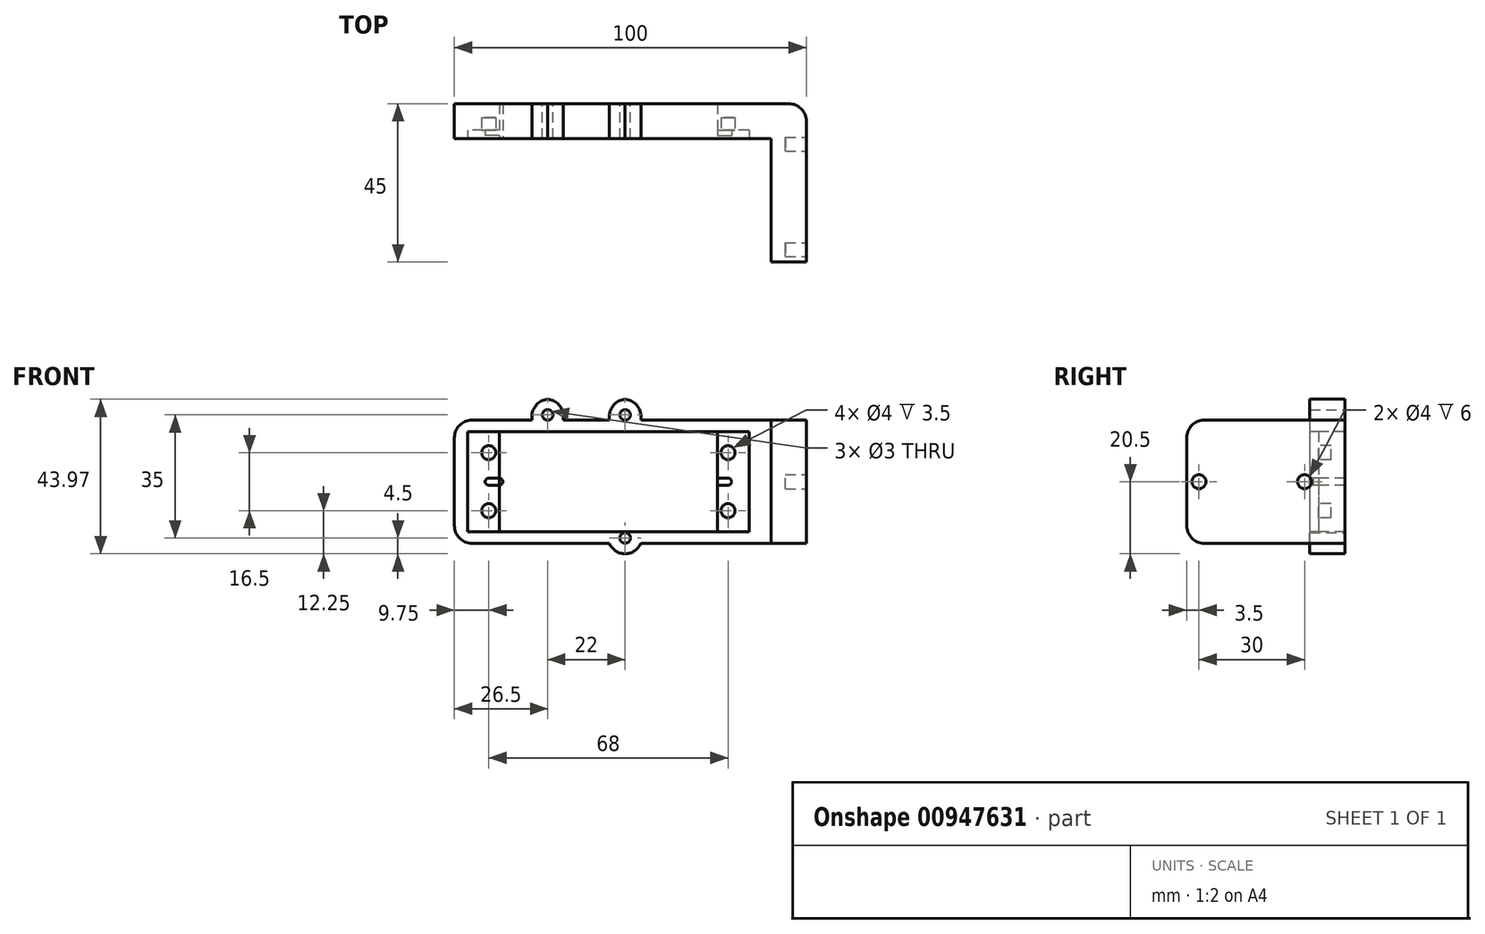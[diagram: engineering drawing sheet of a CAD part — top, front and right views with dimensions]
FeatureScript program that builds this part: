
annotation { "Feature Type Name" : "Feature", "Feature Type Description" : "" }
export const myFeature = defineFeature(function(context is Context, id is Id, definition is map)
    precondition{}
    {
        {
            assignVariable(context, id + "F0", {"name" : "thicc", "anyValue" : 10 * mm});
        }
        {
            var Q0;
            Q0=qCreatedBy(makeId("Top.planeOp"),FACE);
            var sketch = newSketch(context, id + "F1", { "sketchPlane" : qUnion([Q0])});
            skLineSegment(sketch, "E0.bottom", {"start": v(50, 22.5) * mm, "end": v(-50, 22.5) * mm});
            skLineSegment(sketch, "E0.left", {"start": v(50, 22.5) * mm, "end": v(50, -22.5) * mm});
            skPoint(sketch, "E0.middle", {"position": v(0, 0) * mm});
            skLineSegment(sketch, "E1.0", {"start": v(40, 12.5) * mm, "end": v(-50, 12.5) * mm});
            skLineSegment(sketch, "E1.1", {"start": v(40, 12.5) * mm, "end": v(40, -22.5) * mm});
            skLineSegment(sketch, "E2", {"start": v(-50, 22.5) * mm, "end": v(-50, 12.5) * mm});
            skLineSegment(sketch, "E3", {"start": v(40, -22.5) * mm, "end": v(50, -22.5) * mm});
            skSolve(sketch);
        }
        {
            var Q0;
            Q0=makeQuery(id+"F1.imprint","IMPRINT",FACE,{"disambiguationData":[TD([[makeQuery(id+"F1.imprint","IMPRINT",EDGE,{"derivedFrom":sQuery(id+"F1.wireOp",EDGE,"E0.bottom")}),1.0]])]});
            extrude(context, id + "F2", {"entities" : qUnion([Q0]), "depth" : 35 * mm, "offsetDistance" : 25 * mm});
        }
        {
            var Q0;
            Q0=makeQuery(id+"F2.opExtrude","SWEPT_FACE",FACE,{"disambiguationData":[OSD([sQuery(id+"F1.wireOp",EDGE,"E1.0")])]});
            var sketch = newSketch(context, id + "F3", { "sketchPlane" : qUnion([Q0])});
            skLineSegment(sketch, "E4.bottom", {"start": v(30.75, 3.25) * mm, "end": v(-43.25, 3.25) * mm});
            skLineSegment(sketch, "E4.top", {"start": v(30.75, 31.75) * mm, "end": v(-43.25, 31.75) * mm});
            skLineSegment(sketch, "E4.left", {"start": v(30.75, 3.25) * mm, "end": v(30.75, 31.75) * mm, "construction": true});
            skLineSegment(sketch, "E4.right", {"start": v(-43.25, 3.25) * mm, "end": v(-43.25, 31.75) * mm, "construction": true});
            skPoint(sketch, "E4.middle", {"position": v(-6.25, 17.5) * mm});
            skPoint(sketch, "E5", {"position": v(50, 17.5) * mm});
            skPoint(sketch, "E6", {"position": v(0, 0) * mm});
            skLineSegment(sketch, "E7", {"start": v(0, 0) * mm, "end": v(0, 35) * mm, "construction": true});
            skLineSegment(sketch, "E8", {"start": v(-50, 17.5) * mm, "end": v(50, 17.5) * mm, "construction": true});
            skLineSegment(sketch, "E9", {"start": v(24.75, 31.75) * mm, "end": v(24.75, 3.25) * mm});
            skLineSegment(sketch, "E10", {"start": v(-37.25, 31.75) * mm, "end": v(-37.25, 3.25) * mm});
            skLineSegment(sketch, "E11", {"start": v(24.75, 17.5) * mm, "end": v(27.75, 17.5) * mm});
            skLineSegment(sketch, "E12", {"start": v(-37.25, 17.5) * mm, "end": v(-40.25, 17.5) * mm});
            skArc(sketch, "E13.0.startCap", {"start": v(24.75, 16.5) * mm, "mid": v(23.75, 17.5) * mm, "end": v(24.75, 18.5) * mm});
            skArc(sketch, "E13.0.endCap", {"start": v(27.75, 18.5) * mm, "mid": v(28.75, 17.5) * mm, "end": v(27.75, 16.5) * mm});
            skLineSegment(sketch, "E13.0.left", {"start": v(24.75, 18.5) * mm, "end": v(27.75, 18.5) * mm});
            skLineSegment(sketch, "E13.0.right", {"start": v(24.75, 16.5) * mm, "end": v(27.75, 16.5) * mm});
            skArc(sketch, "E13.1.startCap", {"start": v(-37.25, 18.5) * mm, "mid": v(-36.25, 17.5) * mm, "end": v(-37.25, 16.5) * mm});
            skArc(sketch, "E13.1.endCap", {"start": v(-40.25, 16.5) * mm, "mid": v(-41.25, 17.5) * mm, "end": v(-40.25, 18.5) * mm});
            skLineSegment(sketch, "E13.1.left", {"start": v(-37.25, 16.5) * mm, "end": v(-40.25, 16.5) * mm});
            skLineSegment(sketch, "E13.1.right", {"start": v(-37.25, 18.5) * mm, "end": v(-40.25, 18.5) * mm});
            skCircle(sketch, "E14", {"center": v(27.75, 9.25) * mm, "radius": 2 * mm});
            skCircle(sketch, "E15", {"center": v(27.75, 25.75) * mm, "radius": 2 * mm});
            skCircle(sketch, "E16", {"center": v(-40.25, 9.25) * mm, "radius": 2 * mm});
            skCircle(sketch, "E17", {"center": v(-40.25, 25.75) * mm, "radius": 2 * mm});
            skCircle(sketch, "E18", {"center": v(-21.85, 17.5) * mm, "radius": 2.85 * mm, "construction": true});
            skLineSegment(sketch, "E19.bottom", {"start": v(-43.25, 31.75) * mm, "end": v(-46.25, 31.75) * mm});
            skLineSegment(sketch, "E19.top", {"start": v(-46.25, 3.25) * mm, "end": v(-46.25, 3.25) * mm});
            skLineSegment(sketch, "E19.right", {"start": v(-46.25, 31.75) * mm, "end": v(-46.25, 3.25) * mm});
            skLineSegment(sketch, "E20.bottom", {"start": v(30.75, 31.75) * mm, "end": v(33.75, 31.75) * mm});
            skLineSegment(sketch, "E20.top", {"start": v(27.75, 3.25) * mm, "end": v(33.75, 3.25) * mm});
            skLineSegment(sketch, "E20.right", {"start": v(33.75, 31.75) * mm, "end": v(33.75, 3.25) * mm});
            skLineSegment(sketch, "E21", {"start": v(-46.25, 3.25) * mm, "end": v(-43.25, 3.25) * mm});
            skSolve(sketch);
        }
        {
            var Q0;
            {var subQ3=sQuery(id+"F3.wireOp",EDGE,"E13.0.startCap");Q0=makeQuery(id+"F3.imprint","IMPRINT",FACE,{"disambiguationData":[TD([[makeQuery(id+"F3.imprint","IMPRINT",EDGE,{"derivedFrom":subQ3}),1.0]])]});}
            var Q1;
            {var subQ2=sQuery(id+"F3.wireOp",EDGE,"E13.1.startCap");Q1=makeQuery(id+"F3.imprint","IMPRINT",FACE,{"disambiguationData":[TD([[makeQuery(id+"F3.imprint","IMPRINT",EDGE,{"derivedFrom":subQ2}),-1.0]])]});}
            var Q2;
            {var subQ2=sQuery(id+"F3.wireOp",EDGE,"E13.0.startCap");Q2=makeQuery(id+"F3.imprint","IMPRINT",FACE,{"disambiguationData":[TD([[makeQuery(id+"F3.imprint","IMPRINT",EDGE,{"derivedFrom":subQ2}),-1.0]])]});}
            extrude(context, id + "F4", {"entities" : qUnion([Q0, Q1, Q2]), "operationType" : NewBodyOperationType.REMOVE, "endBound" : BoundingType.UP_TO_NEXT, "oppositeDirection" : true, "depth" : 25 * mm, "offsetDistance" : 25 * mm});
        }
        {
            var Q0;
            {var subQ0=sQuery(id+"F3.wireOp",EDGE,"E4.right");Q0=makeQuery(id+"F3.imprint","IMPRINT",FACE,{"disambiguationData":[TD([[makeQuery(id+"F3.imprint","IMPRINT",EDGE,{"derivedFrom":subQ0}),-1.0]])]});}
            var Q1;
            {var subQ0=sQuery(id+"F3.wireOp",EDGE,"E4.left");Q1=makeQuery(id+"F3.imprint","IMPRINT",FACE,{"disambiguationData":[TD([[makeQuery(id+"F3.imprint","IMPRINT",EDGE,{"derivedFrom":subQ0}),1.0]])]});}
            var Q2;
            Q2=makeQuery(id+"F3.imprint","IMPRINT",FACE,{"disambiguationData":[TD([[makeQuery(id+"F3.imprint","IMPRINT",EDGE,{"derivedFrom":sQuery(id+"F3.wireOp",EDGE,"E13.1.endCap")}),-1.0]])]});
            var Q3;
            Q3=makeQuery(id+"F3.imprint","IMPRINT",FACE,{"disambiguationData":[TD([[makeQuery(id+"F3.imprint","IMPRINT",EDGE,{"derivedFrom":sQuery(id+"F3.wireOp",EDGE,"E13.0.endCap")}),-1.0]])]});
            var Q4;
            Q4=makeQuery(id+"F3.imprint","IMPRINT",FACE,{"disambiguationData":[TD([[makeQuery(id+"F3.imprint","IMPRINT",EDGE,{"derivedFrom":sQuery(id+"F3.wireOp",EDGE,"E13.1.endCap")}),1.0]])]});
            var Q5;
            Q5=makeQuery(id+"F3.imprint","IMPRINT",FACE,{"disambiguationData":[TD([[makeQuery(id+"F3.imprint","IMPRINT",EDGE,{"derivedFrom":sQuery(id+"F3.wireOp",EDGE,"E13.0.endCap")}),1.0]])]});
            extrude(context, id + "F5", {"entities" : qUnion([Q0, Q1, Q2, Q3, Q4, Q5]), "operationType" : NewBodyOperationType.REMOVE, "oppositeDirection" : true, "depth" : (getVariable(context, 'thicc') - (6.55 + 2.5) * mm), "offsetDistance" : 25 * mm});
        }
        {
            var Q0;
            Q0=makeQuery(id+"F3.imprint","IMPRINT",FACE,{"disambiguationData":[TD([[makeQuery(id+"F3.imprint","IMPRINT",EDGE,{"derivedFrom":sQuery(id+"F3.wireOp",EDGE,"E13.1.endCap")}),-1.0]])]});
            var Q1;
            Q1=makeQuery(id+"F3.imprint","IMPRINT",FACE,{"disambiguationData":[TD([[makeQuery(id+"F3.imprint","IMPRINT",EDGE,{"derivedFrom":sQuery(id+"F3.wireOp",EDGE,"E13.0.endCap")}),-1.0]])]});
            extrude(context, id + "F6", {"entities" : qUnion([Q0, Q1]), "operationType" : NewBodyOperationType.REMOVE, "oppositeDirection" : true, "depth" : 2.5 * mm, "offsetDistance" : 25 * mm});
        }
        {
            var Q0;
            Q0=makeQuery(id+"F3.imprint","IMPRINT",FACE,{"disambiguationData":[TD([[makeQuery(id+"F3.imprint","IMPRINT",EDGE,{"derivedFrom":sQuery(id+"F3.wireOp",EDGE,"E17")}),1.0]])]});
            var Q1;
            Q1=makeQuery(id+"F3.imprint","IMPRINT",FACE,{"disambiguationData":[TD([[makeQuery(id+"F3.imprint","IMPRINT",EDGE,{"derivedFrom":sQuery(id+"F3.wireOp",EDGE,"E16")}),1.0]])]});
            var Q2;
            Q2=makeQuery(id+"F3.imprint","IMPRINT",FACE,{"disambiguationData":[TD([[makeQuery(id+"F3.imprint","IMPRINT",EDGE,{"derivedFrom":sQuery(id+"F3.wireOp",EDGE,"E14")}),1.0]])]});
            var Q3;
            Q3=makeQuery(id+"F3.imprint","IMPRINT",FACE,{"disambiguationData":[TD([[makeQuery(id+"F3.imprint","IMPRINT",EDGE,{"derivedFrom":sQuery(id+"F3.wireOp",EDGE,"E15")}),1.0]])]});
            extrude(context, id + "F7", {"entities" : qUnion([Q0, Q1, Q2, Q3]), "operationType" : NewBodyOperationType.REMOVE, "oppositeDirection" : true, "depth" : 6 * mm, "offsetDistance" : 25 * mm});
        }
        {
            var Q0;
            Q0=makeQuery(id+"F2.opExtrude","SWEPT_FACE",FACE,{"disambiguationData":[OSD([sQuery(id+"F1.wireOp",EDGE,"E0.bottom")])]});
            var sketch = newSketch(context, id + "F8", { "sketchPlane" : qUnion([Q0])});
            skLineSegment(sketch, "E22.bottom", {"start": v(6, 31.75) * mm, "end": v(-3, 31.75) * mm});
            skLineSegment(sketch, "E22.top", {"start": v(6, 41) * mm, "end": v(-3, 41) * mm});
            skLineSegment(sketch, "E22.left", {"start": v(-3, 31.75) * mm, "end": v(-3, 41) * mm});
            skLineSegment(sketch, "E22.right", {"start": v(6, 31.75) * mm, "end": v(6, 41) * mm});
            skLineSegment(sketch, "E23.bottom", {"start": v(6, 3.25) * mm, "end": v(-3, 3.25) * mm});
            skLineSegment(sketch, "E23.top", {"start": v(6, -3) * mm, "end": v(-3, -3) * mm});
            skLineSegment(sketch, "E23.left", {"start": v(-3, 3.25) * mm, "end": v(-3, -3) * mm});
            skLineSegment(sketch, "E23.right", {"start": v(6, 3.25) * mm, "end": v(6, -3) * mm});
            skCircle(sketch, "E24", {"center": v(1.5, 36.5) * mm, "radius": 1.5 * mm});
            skPoint(sketch, "E24.centerSnap0", {"position": v(1.5, 31.75) * mm});
            skCircle(sketch, "E25", {"center": v(1.5, 1.5) * mm, "radius": 1.5 * mm});
            skPoint(sketch, "E25.centerSnap0", {"position": v(1.5, 3.25) * mm});
            skLineSegment(sketch, "E26", {"start": v(1.5, 1.5) * mm, "end": v(1.5, 3.25) * mm, "construction": true});
            skLineSegment(sketch, "E27", {"start": v(1.5, 36.5) * mm, "end": v(1.5, 31.75) * mm, "construction": true});
            skLineSegment(sketch, "E28.bottom", {"start": v(28, 31.75) * mm, "end": v(19, 31.75) * mm});
            skLineSegment(sketch, "E28.top", {"start": v(28, 41) * mm, "end": v(19, 41) * mm});
            skLineSegment(sketch, "E28.left", {"start": v(28, 31.75) * mm, "end": v(28, 41) * mm});
            skLineSegment(sketch, "E28.right", {"start": v(19, 31.75) * mm, "end": v(19, 41) * mm});
            skCircle(sketch, "E29", {"center": v(23.5, 36.5) * mm, "radius": 1.5 * mm});
            skPoint(sketch, "E29.centerSnap0", {"position": v(23.5, 31.75) * mm});
            skLineSegment(sketch, "E30", {"start": v(23.5, 36.5) * mm, "end": v(23.5, 31.75) * mm, "construction": true});
            skLineSegment(sketch, "E31", {"start": v(23.5, 36.5) * mm, "end": v(1.5, 36.5) * mm, "construction": true});
            skSolve(sketch);
        }
        {
            var Q0;
            Q0 = qSketchRegion(id + "F8", true);
            var Q1;
            Q1=makeQuery(id+"F8.imprint","IMPRINT",FACE,{"disambiguationData":[TD([[makeQuery(id+"F8.imprint","IMPRINT",EDGE,{"derivedFrom":sQuery(id+"F8.wireOp",EDGE,"E24")}),1.0]])]});
            var Q2;
            {var subQ3=sQuery(id+"F1.wireOp",EDGE,"E1.1");var subQ9=sQuery(id+"F1.wireOp",EDGE,"E1.0");Q2=makeQuery(id+"F5.boolean.opBoolean","SPLIT",FACE,{"disambiguationData":[TD([makeQuery(id+"F2.opExtrude","SWEPT_FACE",FACE,{"disambiguationData":[OSD([subQ3])]})])],"derivedFrom":makeQuery(id+"F2.opExtrude","SWEPT_FACE",FACE,{"disambiguationData":[OSD([subQ9])]})});}
            extrude(context, id + "F9", {"entities" : qUnion([Q0, Q1]), "operationType" : NewBodyOperationType.ADD, "endBound" : BoundingType.UP_TO_SURFACE, "oppositeDirection" : true, "depth" : 25 * mm, "endBoundEntityFace" : qUnion([Q2]), "offsetDistance" : 25 * mm});
        }
        {
            var Q0;
            Q0=makeQuery(id+"F8.imprint","IMPRINT",FACE,{"disambiguationData":[TD([[makeQuery(id+"F8.imprint","IMPRINT",EDGE,{"derivedFrom":sQuery(id+"F8.wireOp",EDGE,"E25")}),1.0]])]});
            var Q1;
            Q1=makeQuery(id+"F8.imprint","IMPRINT",FACE,{"disambiguationData":[TD([[makeQuery(id+"F8.imprint","IMPRINT",EDGE,{"derivedFrom":sQuery(id+"F8.wireOp",EDGE,"E24")}),1.0]])]});
            extrude(context, id + "F10", {"entities" : qUnion([Q0, Q1]), "operationType" : NewBodyOperationType.REMOVE, "endBound" : BoundingType.UP_TO_NEXT, "oppositeDirection" : true, "depth" : 25 * mm, "offsetDistance" : 25 * mm});
        }
        {
            var Q0;
            Q0=makeQuery(id+"F2.opExtrude","SWEPT_FACE",FACE,{"disambiguationData":[OSD([sQuery(id+"F1.wireOp",EDGE,"E0.left")])]});
            var sketch = newSketch(context, id + "F11", { "sketchPlane" : qUnion([Q0])});
            skCircle(sketch, "E32", {"center": v(-19, 17.5) * mm, "radius": 2 * mm});
            skPoint(sketch, "E32.centerSnap0", {"position": v(-22.5, 17.5) * mm});
            skCircle(sketch, "E33", {"center": v(11, 17.5) * mm, "radius": 2 * mm});
            skSolve(sketch);
        }
        {
            var Q0;
            Q0 = qSketchRegion(id + "F11", true);
            extrude(context, id + "F12", {"entities" : qUnion([Q0]), "operationType" : NewBodyOperationType.REMOVE, "oppositeDirection" : true, "depth" : 6 * mm, "offsetDistance" : 25 * mm});
        }
        {
            var Q0;
            Q0=makeQuery(id+"F2.opExtrude","CAP_EDGE",EDGE,{"disambiguationData":[OSD([sQuery(id+"F1.wireOp",EDGE,"E2")])],"isStart":false});
            var Q1;
            Q1=makeQuery(id+"F2.opExtrude","CAP_EDGE",EDGE,{"disambiguationData":[OSD([sQuery(id+"F1.wireOp",EDGE,"E2")])],"isStart":true});
            var Q2;
            Q2=makeQuery(id+"F2.opExtrude","CAP_EDGE",EDGE,{"disambiguationData":[OSD([sQuery(id+"F1.wireOp",EDGE,"E3")])],"isStart":false});
            var Q3;
            Q3=makeQuery(id+"F2.opExtrude","CAP_EDGE",EDGE,{"disambiguationData":[OSD([sQuery(id+"F1.wireOp",EDGE,"E3")])],"isStart":true});
            var Q4;
            Q4=makeQuery(id+"F2.opExtrude","SWEPT_EDGE",EDGE,{"disambiguationData":[OSD([sQuery(id+"F1.wireOp",EDGE,"E0.bottom"),sQuery(id+"F1.wireOp",EDGE,"E0.left")])]});
            var Q5;
            Q5=makeQuery(id+"F9.opExtrude","SWEPT_EDGE",EDGE,{"disambiguationData":[OSD([sQuery(id+"F8.wireOp",EDGE,"E23.top"),sQuery(id+"F8.wireOp",EDGE,"E23.left")])]});
            var Q6;
            Q6=makeQuery(id+"F9.opExtrude","SWEPT_EDGE",EDGE,{"disambiguationData":[OSD([sQuery(id+"F8.wireOp",EDGE,"E23.top"),sQuery(id+"F8.wireOp",EDGE,"E23.right")])]});
            var Q7;
            Q7=makeQuery(id+"F9.opExtrude","SWEPT_EDGE",EDGE,{"disambiguationData":[OSD([sQuery(id+"F8.wireOp",EDGE,"E22.top"),sQuery(id+"F8.wireOp",EDGE,"E22.right")])]});
            var Q8;
            Q8=makeQuery(id+"F9.opExtrude","SWEPT_EDGE",EDGE,{"disambiguationData":[OSD([sQuery(id+"F8.wireOp",EDGE,"E22.top"),sQuery(id+"F8.wireOp",EDGE,"E22.left")])]});
            var Q9;
            Q9=makeQuery(id+"F9.opExtrude","SWEPT_EDGE",EDGE,{"disambiguationData":[OSD([sQuery(id+"F8.wireOp",EDGE,"E28.top"),sQuery(id+"F8.wireOp",EDGE,"E28.left")])]});
            var Q10;
            Q10=makeQuery(id+"F9.opExtrude","SWEPT_EDGE",EDGE,{"disambiguationData":[OSD([sQuery(id+"F8.wireOp",EDGE,"E28.top"),sQuery(id+"F8.wireOp",EDGE,"E28.right")])]});
            fillet(context, id + "F13", {"entities" : qUnion([Q0, Q1, Q2, Q3, Q4, Q5, Q6, Q7, Q8, Q9, Q10]), "radius" : 5 * mm, "tangentPropagation" : true, "allowEdgeOverflow" : false});
        }
    });
